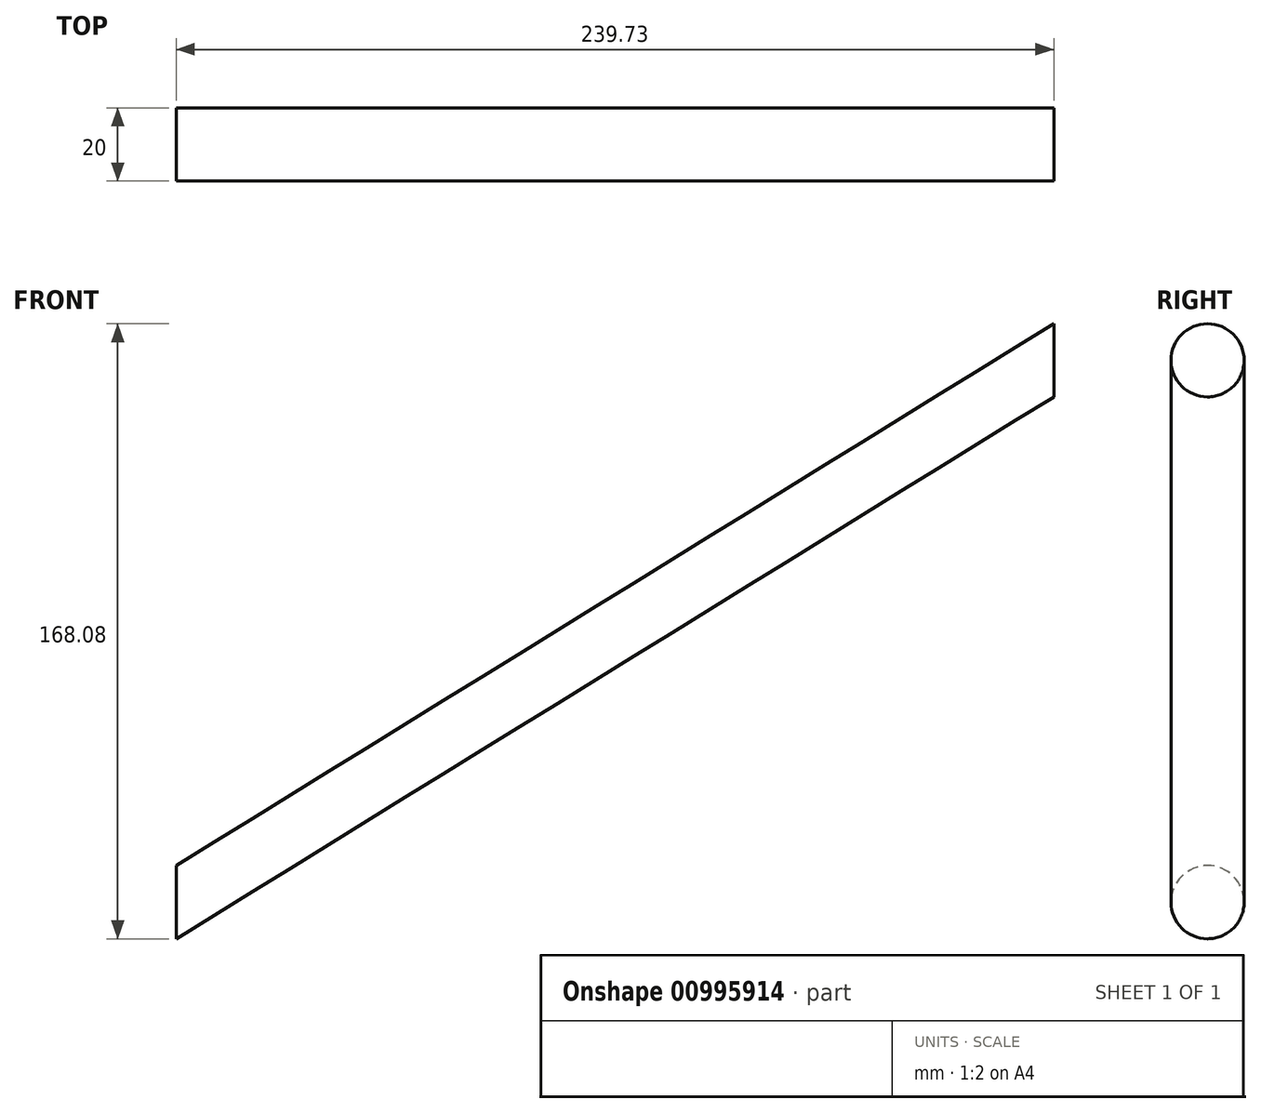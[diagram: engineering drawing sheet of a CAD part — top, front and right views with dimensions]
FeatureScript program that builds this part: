
annotation { "Feature Type Name" : "Feature", "Feature Type Description" : "" }
export const myFeature = defineFeature(function(context is Context, id is Id, definition is map)
    precondition{}
    {
        {
            var Q0;
            Q0=qCreatedBy(makeId("Right.planeOp"),FACE);
            var sketch = newSketch(context, id + "F0", { "sketchPlane" : qUnion([Q0])});
            skCircle(sketch, "E0", {"center": v(0, 41.52) * mm, "radius": 10 * mm});
            skSolve(sketch);
        }
        {
            var Q0;
            Q0=qCreatedBy(makeId("Front.planeOp"),FACE);
            var sketch = newSketch(context, id + "F1", { "sketchPlane" : qUnion([Q0])});
            skLineSegment(sketch, "E1", {"start": v(0, 41.62) * mm, "end": v(-239.73, -106.45) * mm});
            skSolve(sketch);
        }
        {
            var Q0;
            Q0 = qSketchRegion(id + "F0", true);
            var Q1;
            Q1 = qConstructionFilter(qBodyType(qCreatedBy(id + "F1" ,EDGE), BodyType.WIRE), ConstructionObject.NO);
            sweep(context, id + "F2", {"profiles" : qUnion([Q0]), "path" : qUnion([Q1])});
        }
        {
            var Q0;
            Q0=qCreatedBy(makeId("Top.planeOp"),FACE);
            var sketch = newSketch(context, id + "F3", { "sketchPlane" : qUnion([Q0])});
            skEllipse(sketch, "E2", {"center": v(0, 0) * mm, "majorRadius": 19.02 * mm, "minorRadius": 15 * mm, "majorAxis": v(1, 0)});
            skSolve(sketch);
        }
        {
            var Q0;
            Q0=sQuery(id+"F3.wireOp",EDGE,"E2");
            extrude(context, id + "F4", {"bodyType" : ToolBodyType.SURFACE, "surfaceEntities" : qUnion([Q0]), "depth" : 76.8 * mm, "offsetDistance" : 25 * mm});
        }
    });
